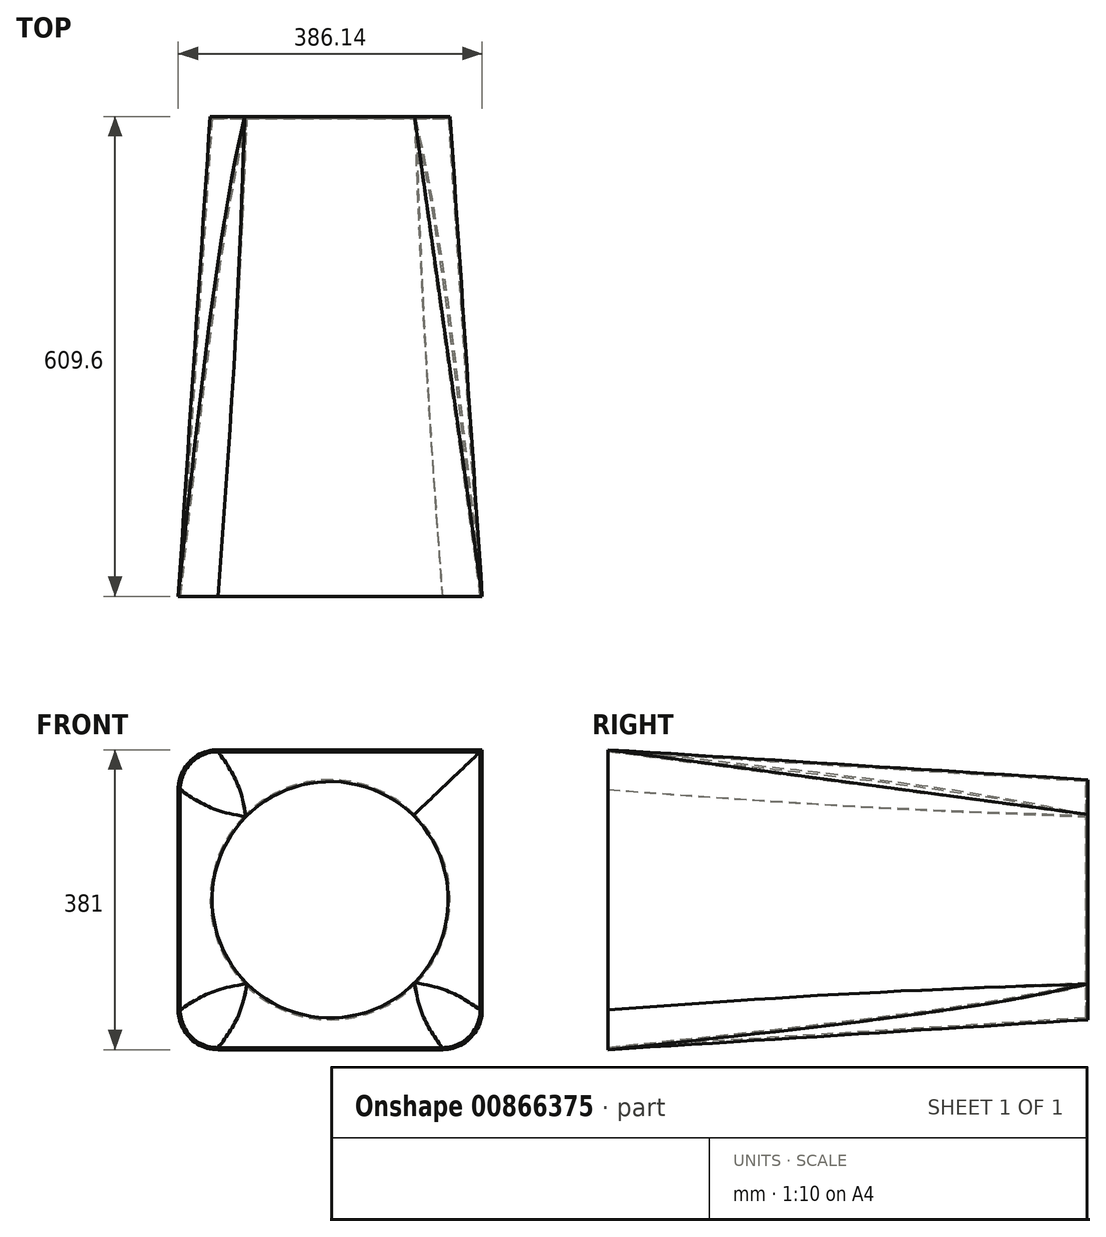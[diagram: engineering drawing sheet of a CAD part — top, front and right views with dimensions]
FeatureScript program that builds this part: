
annotation { "Feature Type Name" : "Feature", "Feature Type Description" : "" }
export const myFeature = defineFeature(function(context is Context, id is Id, definition is map)
    precondition{}
    {
        {
            var Q0;
            Q0=qCreatedBy(makeId("Front.planeOp"),FACE);
            var sketch = newSketch(context, id + "F0", { "sketchPlane" : qUnion([Q0])});
            skCircle(sketch, "E0", {"center": v(0, 0) * mm, "radius": 152.4 * mm});
            skSolve(sketch);
        }
        {
            var Q0;
            Q0=qCreatedBy(makeId("Front.planeOp"),FACE);
            cPlane(context, id + "F1", {"entities" : qUnion([Q0]), "cplaneType" : CPlaneType.OFFSET, "offset" : 609.6 * mm, "width" : 152.4 * mm, "height" : 152.4 * mm});
        }
        {
            var Q0;
            Q0=qCreatedBy(id+"F1.planeOp",FACE);
            var sketch = newSketch(context, id + "F2", { "sketchPlane" : qUnion([Q0])});
            skLineSegment(sketch, "E1.bottom", {"start": v(193.07, -190.5) * mm, "end": v(-193.07, -190.5) * mm});
            skLineSegment(sketch, "E1.top", {"start": v(193.07, 190.5) * mm, "end": v(-193.07, 190.5) * mm});
            skLineSegment(sketch, "E1.left", {"start": v(193.07, -190.5) * mm, "end": v(193.07, 190.5) * mm});
            skLineSegment(sketch, "E1.right", {"start": v(-193.07, -190.5) * mm, "end": v(-193.07, 190.5) * mm});
            skPoint(sketch, "E1.middle", {"position": v(0, 0) * mm});
            skSolve(sketch);
        }
        {
            var Q0;
            Q0=makeQuery(id+"F0.imprint","IMPRINT",FACE,{"disambiguationData":[TD([[makeQuery(id+"F0.imprint","IMPRINT",EDGE,{"derivedFrom":sQuery(id+"F0.wireOp",EDGE,"E0")}),1.0]])]});
            var Q1;
            Q1=makeQuery(id+"F2.imprint","IMPRINT",FACE,{"disambiguationData":[TD([[makeQuery(id+"F2.imprint","IMPRINT",EDGE,{"derivedFrom":sQuery(id+"F2.wireOp",EDGE,"E1.bottom")}),-1.0]])]});
            loft(context, id + "F3", {"sheetProfilesArray" : [{ "sheetProfileEntities" : qUnion([Q0]) }, { "sheetProfileEntities" : qUnion([Q1]) }]});
        }
        {
            var Q0;
            Q0=makeQuery(id+"F3.opLoft","SWEPT_EDGE",EDGE,{"disambiguationData":[OSD([sQuery(id+"F0.wireOp",EDGE,"E0"),sQuery(id+"F2.wireOp",EDGE,"E1.bottom"),sQuery(id+"F2.wireOp",EDGE,"E1.top"),sQuery(id+"F2.wireOp",EDGE,"E1.left")])]});
            var Q1;
            Q1=makeQuery(id+"F3.opLoft","SWEPT_EDGE",EDGE,{"disambiguationData":[OSD([sQuery(id+"F2.wireOp",EDGE,"E1.bottom"),sQuery(id+"F2.wireOp",EDGE,"E1.left")])]});
            var Q2;
            Q2=makeQuery(id+"F3.opLoft","SWEPT_EDGE",EDGE,{"disambiguationData":[OSD([sQuery(id+"F0.wireOp",EDGE,"E0"),sQuery(id+"F2.wireOp",EDGE,"E1.bottom"),sQuery(id+"F2.wireOp",EDGE,"E1.top"),sQuery(id+"F2.wireOp",EDGE,"E1.right")])]});
            var Q3;
            Q3=makeQuery(id+"F3.opLoft","SWEPT_EDGE",EDGE,{"disambiguationData":[OSD([sQuery(id+"F0.wireOp",EDGE,"E0"),sQuery(id+"F2.wireOp",EDGE,"E1.top"),sQuery(id+"F2.wireOp",EDGE,"E1.left"),sQuery(id+"F2.wireOp",EDGE,"E1.right")])]});
            fillet(context, id + "F4", {"entities" : qUnion([Q0, Q1, Q2, Q3]), "radius" : 50.8 * mm, "tangentPropagation" : true, "allowEdgeOverflow" : false});
        }
        {
            var Q0;
            Q0=makeQuery(id+"F3.opLoft","CAP_FACE",FACE,{"disambiguationData":[OSD([makeQuery(id+"F2.imprint","IMPRINT",FACE,{"disambiguationData":[TD([[makeQuery(id+"F2.imprint","IMPRINT",EDGE,{"derivedFrom":sQuery(id+"F2.wireOp",EDGE,"E1.bottom")}),-1.0]])]})])],"isStart":true});
            shell(context, id + "F5", {"entities" : qUnion([Q0]), "thickness" : 2.54 * mm});
        }
    });
